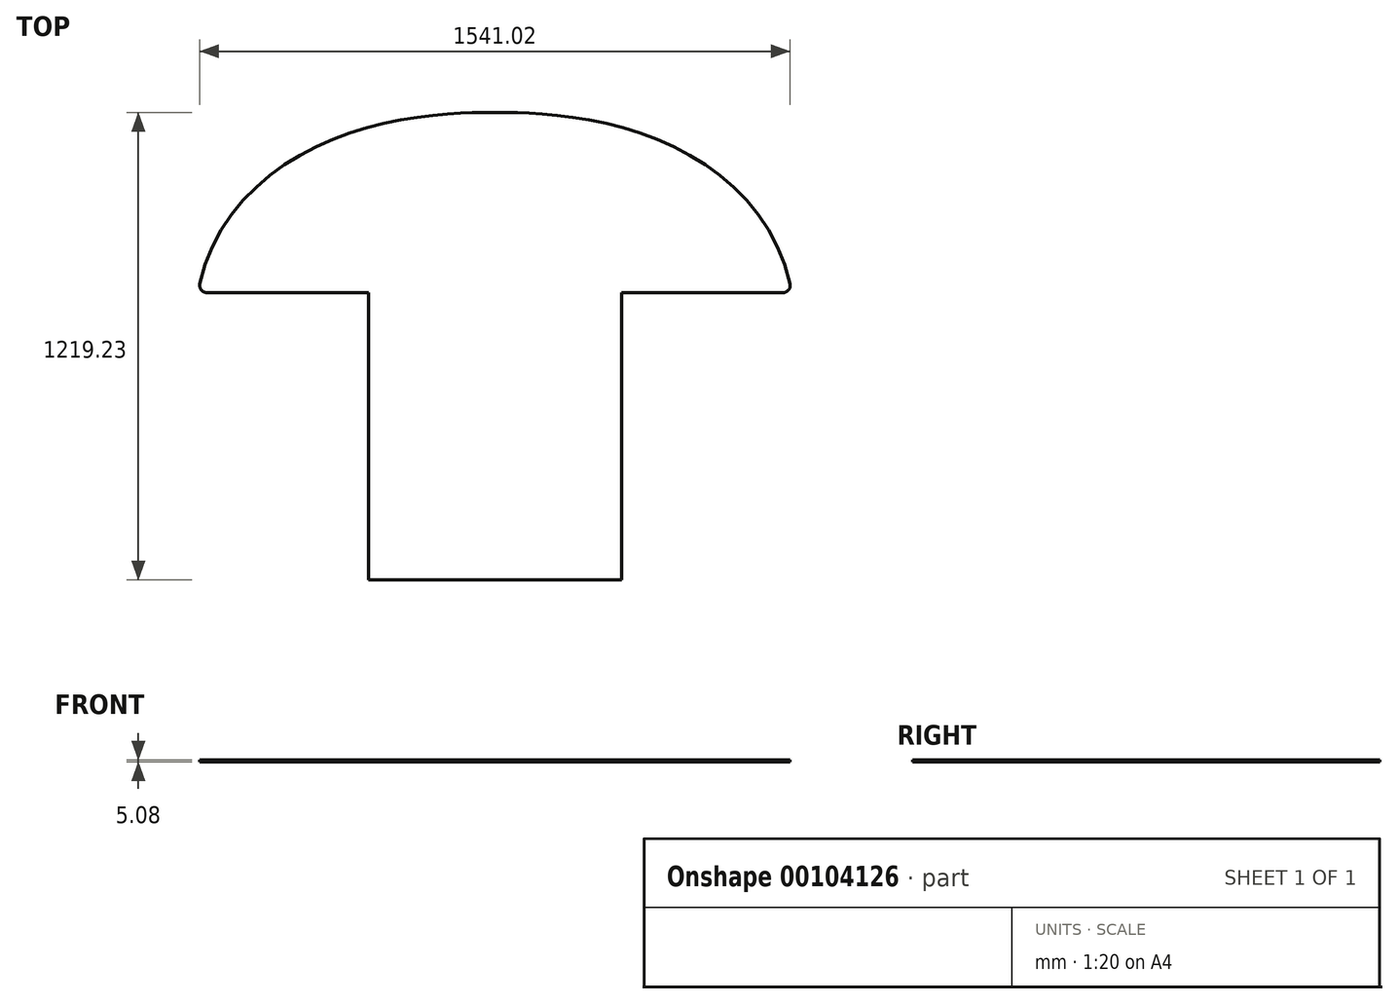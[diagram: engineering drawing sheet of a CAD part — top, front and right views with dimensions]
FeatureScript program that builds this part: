
annotation { "Feature Type Name" : "Feature", "Feature Type Description" : "" }
export const myFeature = defineFeature(function(context is Context, id is Id, definition is map)
    precondition{}
    {
        {
            var Q0;
            Q0=qCreatedBy(makeId("Top.planeOp"),FACE);
            var sketch = newSketch(context, id + "F0", { "sketchPlane" : qUnion([Q0])});
            skLineSegment(sketch, "E0", {"start": v(0, 0) * mm, "end": v(330.2, 0) * mm, "construction": true});
            skLineSegment(sketch, "E1", {"start": v(330.2, 0) * mm, "end": v(330.2, -749.3) * mm});
            skLineSegment(sketch, "E2", {"start": v(330.2, -749.3) * mm, "end": v(0, -749.3) * mm});
            skLineSegment(sketch, "E3", {"start": v(0, -749.3) * mm, "end": v(0, 0) * mm});
            skLineSegment(sketch, "E4", {"start": v(0, 0) * mm, "end": v(0, 469.9) * mm});
            skLineSegment(sketch, "E5", {"start": v(330.2, 0) * mm, "end": v(774.7, 0) * mm});
            skLineSegment(sketch, "E6", {"start": v(774.7, 0) * mm, "end": v(718.27, 320.02) * mm, "construction": true});
            skLineSegment(sketch, "E7", {"start": v(533.4, 0) * mm, "end": v(533.4, 346.08) * mm, "construction": true});
            skLineSegment(sketch, "E8", {"start": v(647.7, 0) * mm, "end": v(647.7, 247.65) * mm, "construction": true});
            skLineSegment(sketch, "E9", {"start": v(330.2, 0) * mm, "end": v(330.2, 431.8) * mm, "construction": true});
            skLineSegment(sketch, "E10", {"start": v(0, 469.9) * mm, "end": v(225.06, 469.9) * mm, "construction": true});
            skFitSpline(sketch, "E11", {"points": [v(0, 469.9) * mm, v(330.2, 431.8) * mm, v(774.7, 0) * mm], "startDerivative": vector(242.1, 0) * mm, "endDerivative": vector(219.59, -1245.35) * mm});
            skSolve(sketch);
        }
        {
            var Q0;
            Q0=makeQuery(id+"F0.imprint","IMPRINT",FACE,{"disambiguationData":[TD([[makeQuery(id+"F0.imprint","IMPRINT",EDGE,{"derivedFrom":sQuery(id+"F0.wireOp",EDGE,"E1")}),-1.0]])]});
            extrude(context, id + "F1", {"entities" : qUnion([Q0]), "depth" : 5.08 * mm});
        }
        {
            var Q0;
            Q0=makeQuery(id+"F1.opExtrude","SWEPT_BODY",BODY,{"disambiguationData":[OSD([sQuery(id+"F0.wireOp",EDGE,"E1"),sQuery(id+"F0.wireOp",EDGE,"E2"),sQuery(id+"F0.wireOp",EDGE,"E3"),sQuery(id+"F0.wireOp",EDGE,"E4"),sQuery(id+"F0.wireOp",EDGE,"E5"),sQuery(id+"F0.wireOp",EDGE,"E11")])]});
            var Q1;
            Q1=makeQuery(id+"F1.opExtrude","SWEPT_FACE",FACE,{"disambiguationData":[OSD([sQuery(id+"F0.wireOp",EDGE,"E3"),sQuery(id+"F0.wireOp",EDGE,"E4")])]});
            mirror(context, id + "F2", {"operationType" : NewBodyOperationType.ADD, "entities" : qUnion([Q0]), "mirrorPlane" : qUnion([Q1])});
        }
        {
            var Q0;
            Q0=makeQuery(id+"F2.opPattern","COPY",EDGE,{"derivedFrom":makeQuery(id+"F1.opExtrude","SWEPT_EDGE",EDGE,{"disambiguationData":[OSD([sQuery(id+"F0.wireOp",EDGE,"E5"),sQuery(id+"F0.wireOp",EDGE,"E11")])]}),"instanceName":"1"});
            var Q1;
            Q1=makeQuery(id+"F1.opExtrude","SWEPT_EDGE",EDGE,{"disambiguationData":[OSD([sQuery(id+"F0.wireOp",EDGE,"E5"),sQuery(id+"F0.wireOp",EDGE,"E11")])]});
            fillet(context, id + "F3", {"entities" : qUnion([Q0, Q1]), "radius" : 19.05 * mm, "tangentPropagation" : true, "allowEdgeOverflow" : false});
        }
    });
